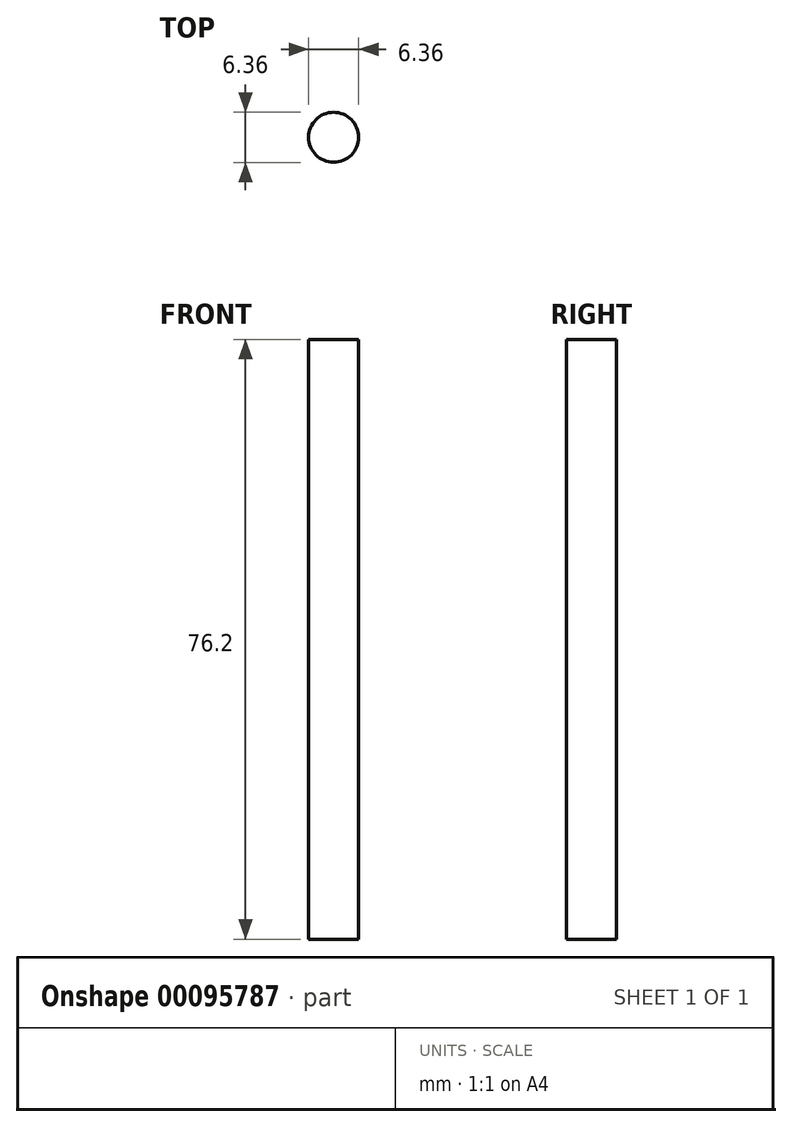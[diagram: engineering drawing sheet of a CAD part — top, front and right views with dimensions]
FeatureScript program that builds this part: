
annotation { "Feature Type Name" : "Feature", "Feature Type Description" : "" }
export const myFeature = defineFeature(function(context is Context, id is Id, definition is map)
    precondition{}
    {
        {
            var Q0;
            Q0=qCreatedBy(makeId("Front.planeOp"),FACE);
            var sketch = newSketch(context, id + "F0", { "sketchPlane" : qUnion([Q0])});
            skLineSegment(sketch, "E0.bottom", {"start": v(0, 0) * mm, "end": v(3.17, 0) * mm});
            skLineSegment(sketch, "E0.top", {"start": v(0, 76.2) * mm, "end": v(3.17, 76.2) * mm});
            skLineSegment(sketch, "E0.left", {"start": v(0, 0) * mm, "end": v(0, 76.2) * mm});
            skLineSegment(sketch, "E0.right", {"start": v(3.18, 0) * mm, "end": v(3.18, 76.2) * mm});
            skSolve(sketch);
        }
        {
            var Q0;
            Q0=makeQuery(id+"F0.imprint","IMPRINT",FACE,{"disambiguationData":[TD([[makeQuery(id+"F0.imprint","IMPRINT",EDGE,{"derivedFrom":sQuery(id+"F0.wireOp",EDGE,"E0.bottom")}),1.0]])]});
            var Q1;
            Q1=sQuery(id+"F0.wireOp",EDGE,"E0.left");
            revolve(context, id + "F1", {"entities" : qUnion([Q0]), "axis" : qUnion([Q1]), "revolveType" : RevolveType.FULL});
        }
    });
